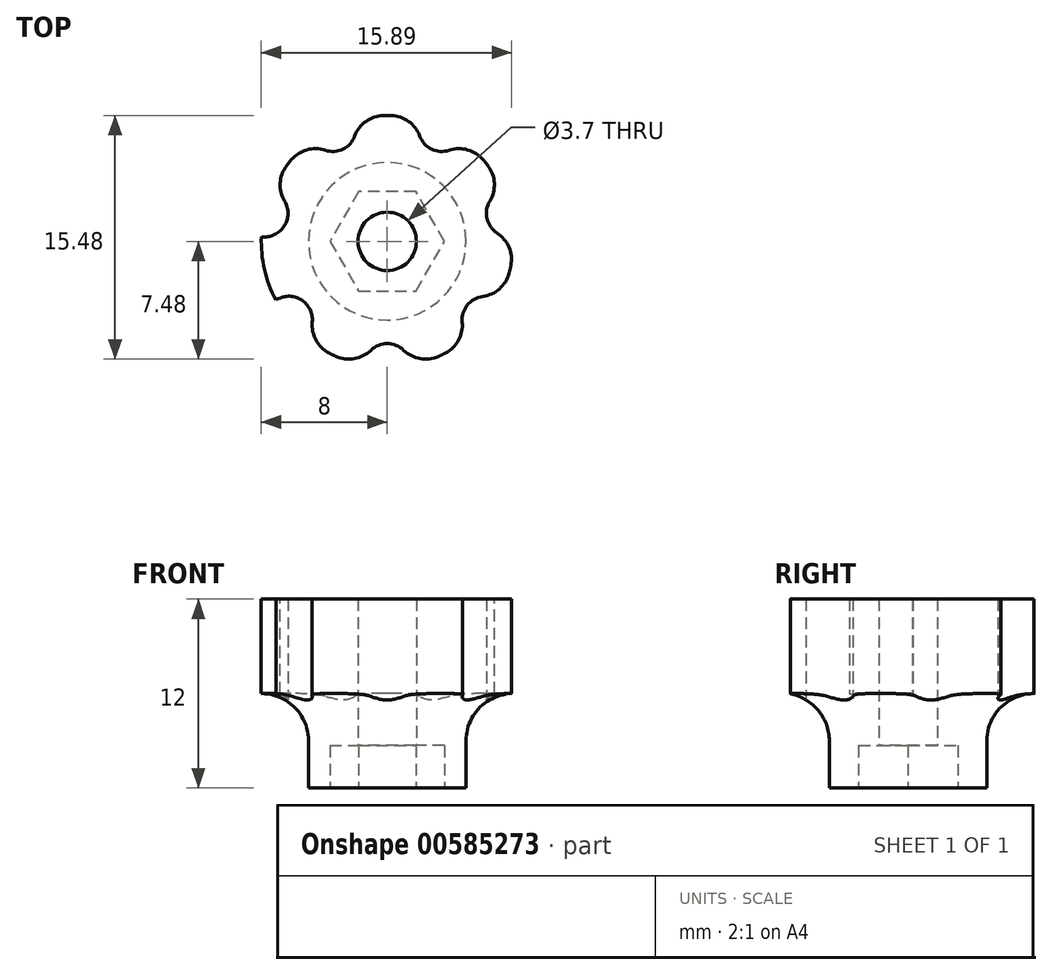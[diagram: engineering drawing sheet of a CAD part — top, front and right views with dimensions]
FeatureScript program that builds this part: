
annotation { "Feature Type Name" : "Feature", "Feature Type Description" : "" }
export const myFeature = defineFeature(function(context is Context, id is Id, definition is map)
    precondition{}
    {
        {
            var Q0;
            Q0=qCreatedBy(makeId("Top.planeOp"),FACE);
            var sketch = newSketch(context, id + "F0", { "sketchPlane" : qUnion([Q0])});
            skCircle(sketch, "E0", {"center": v(0, 0) * mm, "radius": 8 * mm});
            skSolve(sketch);
        }
        {
            var Q0;
            Q0=makeQuery(id+"F0.imprint","IMPRINT",FACE,{"disambiguationData":[TD([[makeQuery(id+"F0.imprint","IMPRINT",EDGE,{"derivedFrom":sQuery(id+"F0.wireOp",EDGE,"E0")}),1.0]])]});
            extrude(context, id + "F1", {"entities" : qUnion([Q0]), "depth" : 12 * mm, "offsetDistance" : 25 * mm});
        }
        {
            var Q0;
            Q0=makeQuery(id+"F1.opExtrude","CAP_FACE",FACE,{"disambiguationData":[OSD([sQuery(id+"F0.wireOp",EDGE,"E0")])],"isStart":true});
            var sketch = newSketch(context, id + "F2", { "sketchPlane" : qUnion([Q0])});
            skCircle(sketch, "E1", {"center": v(0, 0) * mm, "radius": 1.85 * mm});
            skSolve(sketch);
        }
        {
            var Q0;
            Q0=makeQuery(id+"F2.imprint","IMPRINT",FACE,{"disambiguationData":[TD([[makeQuery(id+"F2.imprint","IMPRINT",EDGE,{"derivedFrom":sQuery(id+"F2.wireOp",EDGE,"E1")}),1.0]])]});
            extrude(context, id + "F3", {"entities" : qUnion([Q0]), "operationType" : NewBodyOperationType.REMOVE, "endBound" : BoundingType.THROUGH_ALL, "oppositeDirection" : true, "depth" : 25 * mm, "offsetDistance" : 25 * mm});
        }
        {
            var Q0;
            Q0=makeQuery(id+"F1.opExtrude","CAP_FACE",FACE,{"disambiguationData":[OSD([sQuery(id+"F0.wireOp",EDGE,"E0")])],"isStart":true});
            var sketch = newSketch(context, id + "F4", { "sketchPlane" : qUnion([Q0])});
            skCircle(sketch, "E2.cCircle", {"center": v(0, 0) * mm, "radius": 3.15 * mm, "construction": true});
            skLineSegment(sketch, "E2.0", {"start": v(1.82, -3.15) * mm, "end": v(-1.82, -3.15) * mm});
            skLineSegment(sketch, "E2.1", {"start": v(-1.82, -3.15) * mm, "end": v(-3.64, 0) * mm});
            skLineSegment(sketch, "E2.2", {"start": v(-3.64, 0) * mm, "end": v(-1.82, 3.15) * mm});
            skLineSegment(sketch, "E2.3", {"start": v(-1.82, 3.15) * mm, "end": v(1.82, 3.15) * mm});
            skLineSegment(sketch, "E2.4", {"start": v(1.82, 3.15) * mm, "end": v(3.64, 0) * mm});
            skLineSegment(sketch, "E2.5", {"start": v(3.64, 0) * mm, "end": v(1.82, -3.15) * mm});
            skPoint(sketch, "E2.0.midPoint", {"position": v(0, -3.15) * mm});
            skSolve(sketch);
        }
        {
            var Q0;
            Q0=makeQuery(id+"F4.imprint","IMPRINT",FACE,{"disambiguationData":[TD([[makeQuery(id+"F4.imprint","IMPRINT",EDGE,{"derivedFrom":sQuery(id+"F4.wireOp",EDGE,"E2.0")}),-1.0]])]});
            extrude(context, id + "F5", {"entities" : qUnion([Q0]), "operationType" : NewBodyOperationType.REMOVE, "oppositeDirection" : true, "depth" : 2.7 * mm, "offsetDistance" : 25 * mm});
        }
        {
            var Q0;
            Q0=makeQuery(id+"F1.opExtrude","CAP_FACE",FACE,{"disambiguationData":[OSD([sQuery(id+"F0.wireOp",EDGE,"E0")])],"isStart":true});
            var sketch = newSketch(context, id + "F6", { "sketchPlane" : qUnion([Q0])});
            skCircle(sketch, "E3", {"center": v(0, 0) * mm, "radius": 5 * mm});
            skSolve(sketch);
        }
        {
            var Q0;
            Q0=makeQuery(id+"F6.imprint","IMPRINT",FACE,{"disambiguationData":[TD([[makeQuery(id+"F6.imprint","IMPRINT",EDGE,{"derivedFrom":sQuery(id+"F6.wireOp",EDGE,"E3")}),-1.0]])]});
            extrude(context, id + "F7", {"entities" : qUnion([Q0]), "operationType" : NewBodyOperationType.REMOVE, "oppositeDirection" : true, "depth" : 6 * mm, "offsetDistance" : 25 * mm});
        }
        {
            var Q0;
            Q0=makeQuery(id+"F7.boolean.opBoolean","COPY",FACE,{"derivedFrom":makeQuery(id+"F7.opExtrude","CAP_FACE",FACE,{"disambiguationData":[OSD([sQuery(id+"F0.wireOp",EDGE,"E0"),sQuery(id+"F6.wireOp",EDGE,"E3")])],"isStart":false})});
            var sketch = newSketch(context, id + "F8", { "sketchPlane" : qUnion([Q0])});
            skCircle(sketch, "E4", {"center": v(0, 8) * mm, "radius": 1.5 * mm});
            skCircle(sketch, "E5.1.0", {"center": v(-6.25, 4.99) * mm, "radius": 1.5 * mm});
            skCircle(sketch, "E5.2.0", {"center": v(-7.8, -1.78) * mm, "radius": 1.5 * mm});
            skCircle(sketch, "E5.3.0", {"center": v(-3.47, -7.2) * mm, "radius": 1.5 * mm});
            skCircle(sketch, "E5.4.0", {"center": v(3.47, -7.2) * mm, "radius": 1.5 * mm});
            skCircle(sketch, "E5.5.0", {"center": v(7.8, -1.78) * mm, "radius": 1.5 * mm});
            skCircle(sketch, "E5.6.0", {"center": v(6.25, 4.99) * mm, "radius": 1.5 * mm});
            skPoint(sketch, "E5.center", {"position": v(0, 0) * mm});
            skSolve(sketch);
        }
        {
            var Q0;
            {var subQ0=sQuery(id+"F8.wireOp",EDGE,"E5.1.0");var subQ1=makeQuery(id+"F7.boolean.opBoolean","COPY",EDGE,{"derivedFrom":makeQuery(id+"F7.opExtrude","CAP_EDGE",EDGE,{"disambiguationData":[OSD([sQuery(id+"F0.wireOp",EDGE,"E0")])],"isStart":false})});var subQ2=makeQuery(id+"F8.imprint","INTERSECT",VERTEX,{"disambiguationData":[OD(0.0)],"derivedFrom":[subQ1,subQ0]});Q0=makeQuery(id+"F8.imprint","IMPRINT",FACE,{"disambiguationData":[TD([[makeQuery(id+"F8.imprint","IMPRINT",EDGE,{"disambiguationData":[TD([[subQ2,-1.0]])],"derivedFrom":subQ0}),1.0]])]});}
            var Q1;
            {var subQ0=sQuery(id+"F8.wireOp",EDGE,"E4");var subQ1=makeQuery(id+"F7.boolean.opBoolean","COPY",EDGE,{"derivedFrom":makeQuery(id+"F7.opExtrude","CAP_EDGE",EDGE,{"disambiguationData":[OSD([sQuery(id+"F0.wireOp",EDGE,"E0")])],"isStart":false})});var subQ2=makeQuery(id+"F8.imprint","INTERSECT",VERTEX,{"disambiguationData":[OD(0.0)],"derivedFrom":[subQ1,subQ0]});Q1=makeQuery(id+"F8.imprint","IMPRINT",FACE,{"disambiguationData":[TD([[makeQuery(id+"F8.imprint","IMPRINT",EDGE,{"disambiguationData":[TD([[subQ2,-1.0]])],"derivedFrom":subQ0}),1.0]])]});}
            var Q2;
            {var subQ0=sQuery(id+"F8.wireOp",EDGE,"E5.6.0");var subQ1=makeQuery(id+"F7.boolean.opBoolean","COPY",EDGE,{"derivedFrom":makeQuery(id+"F7.opExtrude","CAP_EDGE",EDGE,{"disambiguationData":[OSD([sQuery(id+"F0.wireOp",EDGE,"E0")])],"isStart":false})});var subQ2=makeQuery(id+"F8.imprint","INTERSECT",VERTEX,{"disambiguationData":[OD(0.0)],"derivedFrom":[subQ1,subQ0]});Q2=makeQuery(id+"F8.imprint","IMPRINT",FACE,{"disambiguationData":[TD([[makeQuery(id+"F8.imprint","IMPRINT",EDGE,{"disambiguationData":[TD([[subQ2,-1.0]])],"derivedFrom":subQ0}),1.0]])]});}
            var Q3;
            {var subQ0=sQuery(id+"F8.wireOp",EDGE,"E5.5.0");var subQ1=makeQuery(id+"F7.boolean.opBoolean","COPY",EDGE,{"derivedFrom":makeQuery(id+"F7.opExtrude","CAP_EDGE",EDGE,{"disambiguationData":[OSD([sQuery(id+"F0.wireOp",EDGE,"E0")])],"isStart":false})});var subQ2=makeQuery(id+"F8.imprint","INTERSECT",VERTEX,{"disambiguationData":[OD(0.0)],"derivedFrom":[subQ1,subQ0]});Q3=makeQuery(id+"F8.imprint","IMPRINT",FACE,{"disambiguationData":[TD([[makeQuery(id+"F8.imprint","IMPRINT",EDGE,{"disambiguationData":[TD([[subQ2,-1.0]])],"derivedFrom":subQ0}),1.0]])]});}
            var Q4;
            {var subQ0=sQuery(id+"F8.wireOp",EDGE,"E5.4.0");var subQ1=makeQuery(id+"F7.boolean.opBoolean","COPY",EDGE,{"derivedFrom":makeQuery(id+"F7.opExtrude","CAP_EDGE",EDGE,{"disambiguationData":[OSD([sQuery(id+"F0.wireOp",EDGE,"E0")])],"isStart":false})});var subQ2=makeQuery(id+"F8.imprint","INTERSECT",VERTEX,{"disambiguationData":[OD(0.0)],"derivedFrom":[subQ1,subQ0]});Q4=makeQuery(id+"F8.imprint","IMPRINT",FACE,{"disambiguationData":[TD([[makeQuery(id+"F8.imprint","IMPRINT",EDGE,{"disambiguationData":[TD([[subQ2,1.0]])],"derivedFrom":subQ0}),1.0]])]});}
            var Q5;
            {var subQ0=sQuery(id+"F8.wireOp",EDGE,"E5.3.0");var subQ1=makeQuery(id+"F7.boolean.opBoolean","COPY",EDGE,{"derivedFrom":makeQuery(id+"F7.opExtrude","CAP_EDGE",EDGE,{"disambiguationData":[OSD([sQuery(id+"F0.wireOp",EDGE,"E0")])],"isStart":false})});var subQ2=makeQuery(id+"F8.imprint","INTERSECT",VERTEX,{"disambiguationData":[OD(0.0)],"derivedFrom":[subQ1,subQ0]});Q5=makeQuery(id+"F8.imprint","IMPRINT",FACE,{"disambiguationData":[TD([[makeQuery(id+"F8.imprint","IMPRINT",EDGE,{"disambiguationData":[TD([[subQ2,1.0]])],"derivedFrom":subQ0}),1.0]])]});}
            var Q6;
            {var subQ0=sQuery(id+"F8.wireOp",EDGE,"E5.2.0");var subQ1=makeQuery(id+"F7.boolean.opBoolean","COPY",EDGE,{"derivedFrom":makeQuery(id+"F7.opExtrude","CAP_EDGE",EDGE,{"disambiguationData":[OSD([sQuery(id+"F0.wireOp",EDGE,"E0")])],"isStart":false})});var subQ2=makeQuery(id+"F8.imprint","INTERSECT",VERTEX,{"disambiguationData":[OD(0.0)],"derivedFrom":[subQ1,subQ0]});Q6=makeQuery(id+"F8.imprint","IMPRINT",FACE,{"disambiguationData":[TD([[makeQuery(id+"F8.imprint","IMPRINT",EDGE,{"disambiguationData":[TD([[subQ2,1.0]])],"derivedFrom":subQ0}),1.0]])]});}
            extrude(context, id + "F9", {"entities" : qUnion([Q0, Q1, Q2, Q3, Q4, Q5, Q6]), "operationType" : NewBodyOperationType.REMOVE, "endBound" : BoundingType.THROUGH_ALL, "oppositeDirection" : true, "depth" : 25 * mm, "offsetDistance" : 25 * mm});
        }
        {
            var Q0;
            {var subQ0=sQuery(id+"F8.wireOp",EDGE,"E4");var subQ1=sQuery(id+"F0.wireOp",EDGE,"E0");Q0=makeQuery(id+"F9.boolean.opBoolean","COPY",EDGE,{"derivedFrom":makeQuery(id+"F9.opExtrude","SWEPT_EDGE",EDGE,{"disambiguationData":[OSD([subQ1,subQ0]),TDD([makeQuery(id+"F8.imprint","INTERSECT",VERTEX,{"disambiguationData":[OD(0.0)],"derivedFrom":[makeQuery(id+"F7.boolean.opBoolean","COPY",EDGE,{"derivedFrom":makeQuery(id+"F7.opExtrude","CAP_EDGE",EDGE,{"disambiguationData":[OSD([subQ1])],"isStart":false})}),subQ0]})])]})});}
            var Q1;
            {var subQ0=sQuery(id+"F8.wireOp",EDGE,"E4");var subQ1=sQuery(id+"F0.wireOp",EDGE,"E0");Q1=makeQuery(id+"F9.boolean.opBoolean","COPY",EDGE,{"derivedFrom":makeQuery(id+"F9.opExtrude","SWEPT_EDGE",EDGE,{"disambiguationData":[OSD([subQ1,subQ0]),TDD([makeQuery(id+"F8.imprint","INTERSECT",VERTEX,{"disambiguationData":[OD(1.0)],"derivedFrom":[makeQuery(id+"F7.boolean.opBoolean","COPY",EDGE,{"derivedFrom":makeQuery(id+"F7.opExtrude","CAP_EDGE",EDGE,{"disambiguationData":[OSD([subQ1])],"isStart":false})}),subQ0]})])]})});}
            var Q2;
            {var subQ0=sQuery(id+"F8.wireOp",EDGE,"E5.6.0");var subQ1=sQuery(id+"F0.wireOp",EDGE,"E0");Q2=makeQuery(id+"F9.boolean.opBoolean","COPY",EDGE,{"derivedFrom":makeQuery(id+"F9.opExtrude","SWEPT_EDGE",EDGE,{"disambiguationData":[OSD([subQ1,subQ0]),TDD([makeQuery(id+"F8.imprint","INTERSECT",VERTEX,{"disambiguationData":[OD(0.0)],"derivedFrom":[makeQuery(id+"F7.boolean.opBoolean","COPY",EDGE,{"derivedFrom":makeQuery(id+"F7.opExtrude","CAP_EDGE",EDGE,{"disambiguationData":[OSD([subQ1])],"isStart":false})}),subQ0]})])]})});}
            var Q3;
            {var subQ0=sQuery(id+"F8.wireOp",EDGE,"E5.6.0");var subQ1=sQuery(id+"F0.wireOp",EDGE,"E0");Q3=makeQuery(id+"F9.boolean.opBoolean","COPY",EDGE,{"derivedFrom":makeQuery(id+"F9.opExtrude","SWEPT_EDGE",EDGE,{"disambiguationData":[OSD([subQ1,subQ0]),TDD([makeQuery(id+"F8.imprint","INTERSECT",VERTEX,{"disambiguationData":[OD(1.0)],"derivedFrom":[makeQuery(id+"F7.boolean.opBoolean","COPY",EDGE,{"derivedFrom":makeQuery(id+"F7.opExtrude","CAP_EDGE",EDGE,{"disambiguationData":[OSD([subQ1])],"isStart":false})}),subQ0]})])]})});}
            var Q4;
            {var subQ0=sQuery(id+"F8.wireOp",EDGE,"E5.5.0");var subQ1=sQuery(id+"F0.wireOp",EDGE,"E0");Q4=makeQuery(id+"F9.boolean.opBoolean","COPY",EDGE,{"derivedFrom":makeQuery(id+"F9.opExtrude","SWEPT_EDGE",EDGE,{"disambiguationData":[OSD([subQ1,subQ0]),TDD([makeQuery(id+"F8.imprint","INTERSECT",VERTEX,{"disambiguationData":[OD(0.0)],"derivedFrom":[makeQuery(id+"F7.boolean.opBoolean","COPY",EDGE,{"derivedFrom":makeQuery(id+"F7.opExtrude","CAP_EDGE",EDGE,{"disambiguationData":[OSD([subQ1])],"isStart":false})}),subQ0]})])]})});}
            var Q5;
            {var subQ0=sQuery(id+"F8.wireOp",EDGE,"E5.5.0");var subQ1=sQuery(id+"F0.wireOp",EDGE,"E0");Q5=makeQuery(id+"F9.boolean.opBoolean","COPY",EDGE,{"derivedFrom":makeQuery(id+"F9.opExtrude","SWEPT_EDGE",EDGE,{"disambiguationData":[OSD([subQ1,subQ0]),TDD([makeQuery(id+"F8.imprint","INTERSECT",VERTEX,{"disambiguationData":[OD(1.0)],"derivedFrom":[makeQuery(id+"F7.boolean.opBoolean","COPY",EDGE,{"derivedFrom":makeQuery(id+"F7.opExtrude","CAP_EDGE",EDGE,{"disambiguationData":[OSD([subQ1])],"isStart":false})}),subQ0]})])]})});}
            var Q6;
            {var subQ0=sQuery(id+"F8.wireOp",EDGE,"E5.4.0");var subQ1=sQuery(id+"F0.wireOp",EDGE,"E0");Q6=makeQuery(id+"F9.boolean.opBoolean","COPY",EDGE,{"derivedFrom":makeQuery(id+"F9.opExtrude","SWEPT_EDGE",EDGE,{"disambiguationData":[OSD([subQ1,subQ0]),TDD([makeQuery(id+"F8.imprint","INTERSECT",VERTEX,{"disambiguationData":[OD(1.0)],"derivedFrom":[makeQuery(id+"F7.boolean.opBoolean","COPY",EDGE,{"derivedFrom":makeQuery(id+"F7.opExtrude","CAP_EDGE",EDGE,{"disambiguationData":[OSD([subQ1])],"isStart":false})}),subQ0]})])]})});}
            var Q7;
            {var subQ0=sQuery(id+"F8.wireOp",EDGE,"E5.4.0");var subQ1=sQuery(id+"F0.wireOp",EDGE,"E0");Q7=makeQuery(id+"F9.boolean.opBoolean","COPY",EDGE,{"derivedFrom":makeQuery(id+"F9.opExtrude","SWEPT_EDGE",EDGE,{"disambiguationData":[OSD([subQ1,subQ0]),TDD([makeQuery(id+"F8.imprint","INTERSECT",VERTEX,{"disambiguationData":[OD(0.0)],"derivedFrom":[makeQuery(id+"F7.boolean.opBoolean","COPY",EDGE,{"derivedFrom":makeQuery(id+"F7.opExtrude","CAP_EDGE",EDGE,{"disambiguationData":[OSD([subQ1])],"isStart":false})}),subQ0]})])]})});}
            var Q8;
            {var subQ0=sQuery(id+"F8.wireOp",EDGE,"E5.3.0");var subQ1=sQuery(id+"F0.wireOp",EDGE,"E0");Q8=makeQuery(id+"F9.boolean.opBoolean","COPY",EDGE,{"derivedFrom":makeQuery(id+"F9.opExtrude","SWEPT_EDGE",EDGE,{"disambiguationData":[OSD([subQ1,subQ0]),TDD([makeQuery(id+"F8.imprint","INTERSECT",VERTEX,{"disambiguationData":[OD(1.0)],"derivedFrom":[makeQuery(id+"F7.boolean.opBoolean","COPY",EDGE,{"derivedFrom":makeQuery(id+"F7.opExtrude","CAP_EDGE",EDGE,{"disambiguationData":[OSD([subQ1])],"isStart":false})}),subQ0]})])]})});}
            var Q9;
            {var subQ0=sQuery(id+"F8.wireOp",EDGE,"E5.3.0");var subQ1=sQuery(id+"F0.wireOp",EDGE,"E0");Q9=makeQuery(id+"F9.boolean.opBoolean","COPY",EDGE,{"derivedFrom":makeQuery(id+"F9.opExtrude","SWEPT_EDGE",EDGE,{"disambiguationData":[OSD([subQ1,subQ0]),TDD([makeQuery(id+"F8.imprint","INTERSECT",VERTEX,{"disambiguationData":[OD(0.0)],"derivedFrom":[makeQuery(id+"F7.boolean.opBoolean","COPY",EDGE,{"derivedFrom":makeQuery(id+"F7.opExtrude","CAP_EDGE",EDGE,{"disambiguationData":[OSD([subQ1])],"isStart":false})}),subQ0]})])]})});}
            var Q10;
            {var subQ0=sQuery(id+"F8.wireOp",EDGE,"E5.2.0");var subQ1=sQuery(id+"F0.wireOp",EDGE,"E0");Q10=makeQuery(id+"F9.boolean.opBoolean","COPY",EDGE,{"derivedFrom":makeQuery(id+"F9.opExtrude","SWEPT_EDGE",EDGE,{"disambiguationData":[OSD([subQ1,subQ0]),TDD([makeQuery(id+"F8.imprint","INTERSECT",VERTEX,{"disambiguationData":[OD(1.0)],"derivedFrom":[makeQuery(id+"F7.boolean.opBoolean","COPY",EDGE,{"derivedFrom":makeQuery(id+"F7.opExtrude","CAP_EDGE",EDGE,{"disambiguationData":[OSD([subQ1])],"isStart":false})}),subQ0]})])]})});}
            var Q11;
            {var subQ0=sQuery(id+"F8.wireOp",EDGE,"E5.2.0");var subQ1=sQuery(id+"F0.wireOp",EDGE,"E0");Q11=makeQuery(id+"F9.boolean.opBoolean","COPY",EDGE,{"derivedFrom":makeQuery(id+"F9.opExtrude","SWEPT_EDGE",EDGE,{"disambiguationData":[OSD([subQ1,subQ0]),TDD([makeQuery(id+"F8.imprint","INTERSECT",VERTEX,{"disambiguationData":[OD(0.0)],"derivedFrom":[makeQuery(id+"F7.boolean.opBoolean","COPY",EDGE,{"derivedFrom":makeQuery(id+"F7.opExtrude","CAP_EDGE",EDGE,{"disambiguationData":[OSD([subQ1])],"isStart":false})}),subQ0]})])]})});}
            var Q12;
            {var subQ0=sQuery(id+"F8.wireOp",EDGE,"E5.1.0");var subQ1=sQuery(id+"F0.wireOp",EDGE,"E0");Q12=makeQuery(id+"F9.boolean.opBoolean","COPY",EDGE,{"derivedFrom":makeQuery(id+"F9.opExtrude","SWEPT_EDGE",EDGE,{"disambiguationData":[OSD([subQ1,subQ0]),TDD([makeQuery(id+"F8.imprint","INTERSECT",VERTEX,{"disambiguationData":[OD(0.0)],"derivedFrom":[makeQuery(id+"F7.boolean.opBoolean","COPY",EDGE,{"derivedFrom":makeQuery(id+"F7.opExtrude","CAP_EDGE",EDGE,{"disambiguationData":[OSD([subQ1])],"isStart":false})}),subQ0]})])]})});}
            var Q13;
            {var subQ0=sQuery(id+"F8.wireOp",EDGE,"E5.1.0");var subQ1=sQuery(id+"F0.wireOp",EDGE,"E0");Q13=makeQuery(id+"F9.boolean.opBoolean","COPY",EDGE,{"derivedFrom":makeQuery(id+"F9.opExtrude","SWEPT_EDGE",EDGE,{"disambiguationData":[OSD([subQ1,subQ0]),TDD([makeQuery(id+"F8.imprint","INTERSECT",VERTEX,{"disambiguationData":[OD(1.0)],"derivedFrom":[makeQuery(id+"F7.boolean.opBoolean","COPY",EDGE,{"derivedFrom":makeQuery(id+"F7.opExtrude","CAP_EDGE",EDGE,{"disambiguationData":[OSD([subQ1])],"isStart":false})}),subQ0]})])]})});}
            fillet(context, id + "F10", {"entities" : qUnion([Q0, Q1, Q2, Q3, Q4, Q5, Q6, Q7, Q8, Q9, Q10, Q11, Q12, Q13]), "radius" : 2 * mm, "tangentPropagation" : true, "allowEdgeOverflow" : false});
        }
        {
            var Q0;
            Q0=makeQuery(id+"F7.boolean.opBoolean","COPY",EDGE,{"derivedFrom":makeQuery(id+"F7.opExtrude","CAP_EDGE",EDGE,{"disambiguationData":[OSD([sQuery(id+"F6.wireOp",EDGE,"E3")])],"isStart":false})});
            fillet(context, id + "F11", {"entities" : qUnion([Q0]), "radius" : 3 * mm, "tangentPropagation" : true, "allowEdgeOverflow" : false});
        }
    });
